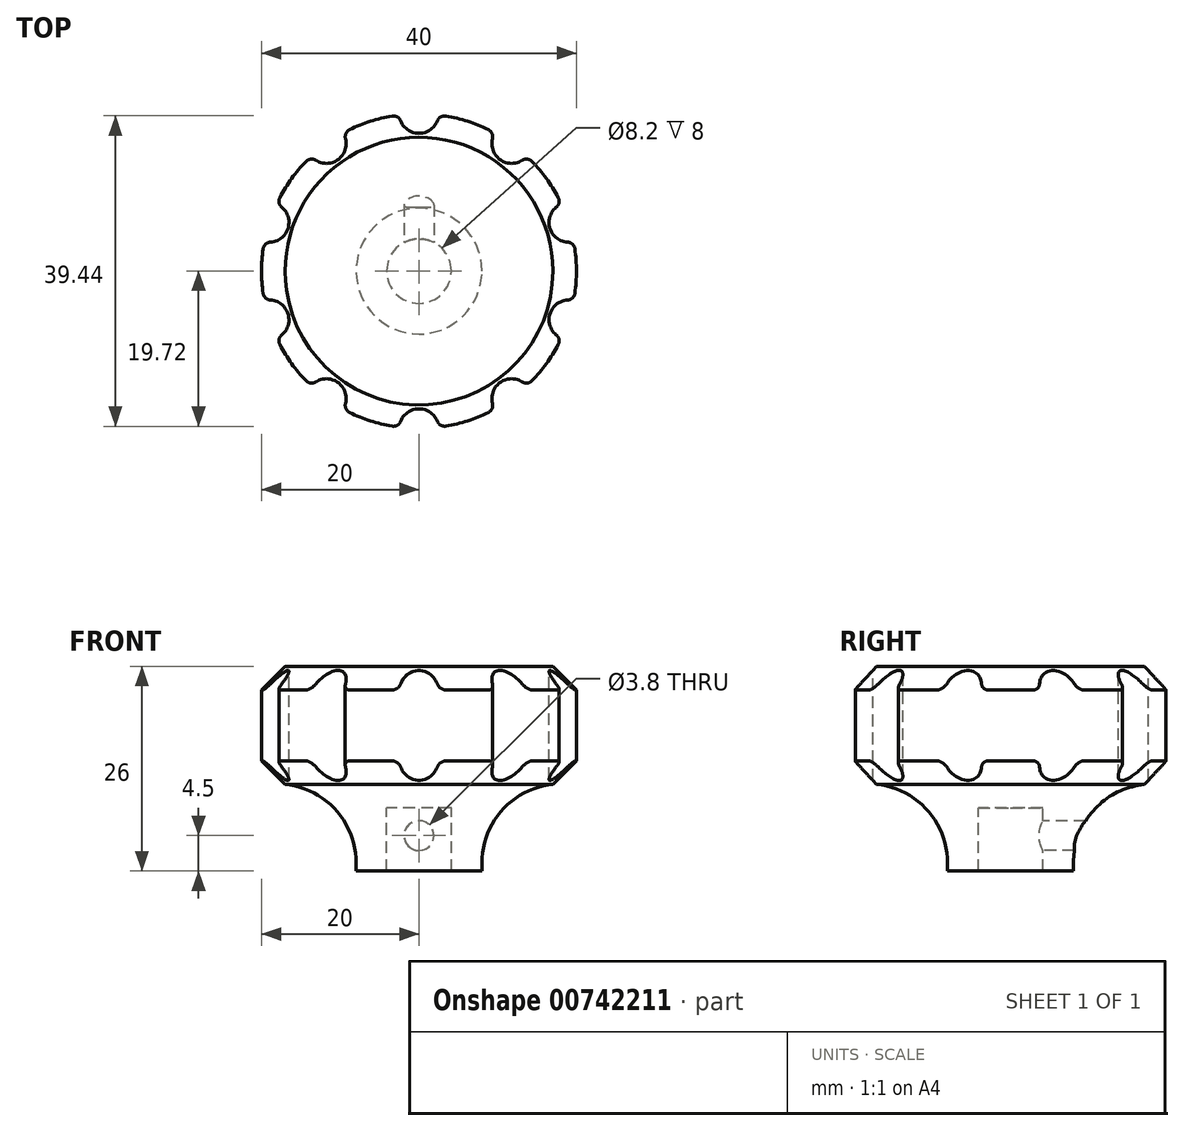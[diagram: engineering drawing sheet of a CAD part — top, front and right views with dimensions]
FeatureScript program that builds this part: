
annotation { "Feature Type Name" : "Feature", "Feature Type Description" : "" }
export const myFeature = defineFeature(function(context is Context, id is Id, definition is map)
    precondition{}
    {
        {
            var Q0;
            Q0=qCreatedBy(makeId("Front.planeOp"),FACE);
            var sketch = newSketch(context, id + "F0", { "sketchPlane" : qUnion([Q0])});
            skLineSegment(sketch, "E0", {"start": v(0, 8) * mm, "end": v(0, 26) * mm});
            skLineSegment(sketch, "E1", {"start": v(0, 26) * mm, "end": v(-20, 26) * mm});
            skLineSegment(sketch, "E2", {"start": v(-20, 26) * mm, "end": v(-20, 11) * mm});
            skLineSegment(sketch, "E3", {"start": v(-20, 11) * mm, "end": v(-8, 11) * mm});
            skLineSegment(sketch, "E4", {"start": v(-8, 11) * mm, "end": v(-8, 0) * mm});
            skLineSegment(sketch, "E5", {"start": v(-8, 0) * mm, "end": v(-4.1, 0) * mm});
            skLineSegment(sketch, "E6", {"start": v(-4.1, 0) * mm, "end": v(-4.1, 8) * mm});
            skLineSegment(sketch, "E7", {"start": v(-4.1, 8) * mm, "end": v(0, 8) * mm});
            skLineSegment(sketch, "E8", {"start": v(0, 48.85) * mm, "end": v(0, -40.92) * mm, "construction": true});
            skSolve(sketch);
        }
        {
            var Q0;
            Q0 = qSketchRegion(id + "F0", true);
            var Q1;
            Q1=sQuery(id+"F0.wireOp",EDGE,"E8");
            revolve(context, id + "F1", {"surfaceOperationType" : NewSurfaceOperationType.NEW, "entities" : qUnion([Q0]), "axis" : qUnion([Q1]), "revolveType" : RevolveType.FULL});
        }
        {
            var Q0;
            Q0=makeQuery(id+"F1.opRevolve","SWEPT_FACE",FACE,{"disambiguationData":[OSD([sQuery(id+"F0.wireOp",EDGE,"E1")])]});
            var sketch = newSketch(context, id + "F2", { "sketchPlane" : qUnion([Q0])});
            skCircle(sketch, "E9", {"center": v(0, 20) * mm, "radius": 2.5 * mm});
            skCircle(sketch, "E10.1.0", {"center": v(-11.76, 16.18) * mm, "radius": 2.5 * mm});
            skCircle(sketch, "E10.2.0", {"center": v(-19.02, 6.18) * mm, "radius": 2.5 * mm});
            skCircle(sketch, "E10.3.0", {"center": v(-19.02, -6.18) * mm, "radius": 2.5 * mm});
            skCircle(sketch, "E10.4.0", {"center": v(-11.76, -16.18) * mm, "radius": 2.5 * mm});
            skCircle(sketch, "E10.5.0", {"center": v(0, -20) * mm, "radius": 2.5 * mm});
            skCircle(sketch, "E10.6.0", {"center": v(11.76, -16.18) * mm, "radius": 2.5 * mm});
            skCircle(sketch, "E10.7.0", {"center": v(19.02, -6.18) * mm, "radius": 2.5 * mm});
            skCircle(sketch, "E10.8.0", {"center": v(19.02, 6.18) * mm, "radius": 2.5 * mm});
            skCircle(sketch, "E10.9.0", {"center": v(11.76, 16.18) * mm, "radius": 2.5 * mm});
            skPoint(sketch, "E10.center", {"position": v(0, 0) * mm});
            skSolve(sketch);
        }
        {
            var Q0;
            Q0=makeQuery(id+"F1.opRevolve","SWEPT_EDGE",EDGE,{"disambiguationData":[OSD([sQuery(id+"F0.wireOp",EDGE,"E1"),sQuery(id+"F0.wireOp",EDGE,"E2")])]});
            var Q1;
            Q1=makeQuery(id+"F1.opRevolve","SWEPT_EDGE",EDGE,{"disambiguationData":[OSD([sQuery(id+"F0.wireOp",EDGE,"E2"),sQuery(id+"F0.wireOp",EDGE,"E3")])]});
            chamfer(context, id + "F3", {"entities" : qUnion([Q0, Q1]), "width" : 3 * mm, "tangentPropagation" : true});
        }
        {
            var Q0;
            Q0 = qSketchRegion(id + "F2", true);
            extrude(context, id + "F4", {"entities" : qUnion([Q0]), "operationType" : NewBodyOperationType.REMOVE, "oppositeDirection" : true, "depth" : 25 * mm, "offsetDistance" : 25 * mm});
        }
        {
            var Q0;
            Q0=makeQuery(id+"F4.boolean.opBoolean","INTERSECT",EDGE,{"disambiguationData":[OD(0.0)],"derivedFrom":[makeQuery(id+"F1.opRevolve","SWEPT_FACE",FACE,{"disambiguationData":[OSD([sQuery(id+"F0.wireOp",EDGE,"E2")])]}),makeQuery(id+"F4.opExtrude","SWEPT_FACE",FACE,{"disambiguationData":[OSD([sQuery(id+"F2.wireOp",EDGE,"E10.4.0")])]})]});
            var Q1;
            Q1=makeQuery(id+"F4.boolean.opBoolean","INTERSECT",EDGE,{"disambiguationData":[OD(1.0)],"derivedFrom":[makeQuery(id+"F1.opRevolve","SWEPT_FACE",FACE,{"disambiguationData":[OSD([sQuery(id+"F0.wireOp",EDGE,"E2")])]}),makeQuery(id+"F4.opExtrude","SWEPT_FACE",FACE,{"disambiguationData":[OSD([sQuery(id+"F2.wireOp",EDGE,"E10.3.0")])]})]});
            var Q2;
            Q2=makeQuery(id+"F4.boolean.opBoolean","INTERSECT",EDGE,{"disambiguationData":[OD(0.0)],"derivedFrom":[makeQuery(id+"F1.opRevolve","SWEPT_FACE",FACE,{"disambiguationData":[OSD([sQuery(id+"F0.wireOp",EDGE,"E2")])]}),makeQuery(id+"F4.opExtrude","SWEPT_FACE",FACE,{"disambiguationData":[OSD([sQuery(id+"F2.wireOp",EDGE,"E10.3.0")])]})]});
            var Q3;
            Q3=makeQuery(id+"F4.boolean.opBoolean","INTERSECT",EDGE,{"disambiguationData":[OD(1.0)],"derivedFrom":[makeQuery(id+"F1.opRevolve","SWEPT_FACE",FACE,{"disambiguationData":[OSD([sQuery(id+"F0.wireOp",EDGE,"E2")])]}),makeQuery(id+"F4.opExtrude","SWEPT_FACE",FACE,{"disambiguationData":[OSD([sQuery(id+"F2.wireOp",EDGE,"E10.2.0")])]})]});
            var Q4;
            Q4=makeQuery(id+"F4.boolean.opBoolean","INTERSECT",EDGE,{"disambiguationData":[OD(0.0)],"derivedFrom":[makeQuery(id+"F1.opRevolve","SWEPT_FACE",FACE,{"disambiguationData":[OSD([sQuery(id+"F0.wireOp",EDGE,"E2")])]}),makeQuery(id+"F4.opExtrude","SWEPT_FACE",FACE,{"disambiguationData":[OSD([sQuery(id+"F2.wireOp",EDGE,"E10.2.0")])]})]});
            var Q5;
            Q5=makeQuery(id+"F4.boolean.opBoolean","INTERSECT",EDGE,{"disambiguationData":[OD(1.0)],"derivedFrom":[makeQuery(id+"F1.opRevolve","SWEPT_FACE",FACE,{"disambiguationData":[OSD([sQuery(id+"F0.wireOp",EDGE,"E2")])]}),makeQuery(id+"F4.opExtrude","SWEPT_FACE",FACE,{"disambiguationData":[OSD([sQuery(id+"F2.wireOp",EDGE,"E10.1.0")])]})]});
            var Q6;
            Q6=makeQuery(id+"F4.boolean.opBoolean","INTERSECT",EDGE,{"disambiguationData":[OD(0.0)],"derivedFrom":[makeQuery(id+"F1.opRevolve","SWEPT_FACE",FACE,{"disambiguationData":[OSD([sQuery(id+"F0.wireOp",EDGE,"E2")])]}),makeQuery(id+"F4.opExtrude","SWEPT_FACE",FACE,{"disambiguationData":[OSD([sQuery(id+"F2.wireOp",EDGE,"E10.1.0")])]})]});
            var Q7;
            Q7=makeQuery(id+"F4.boolean.opBoolean","INTERSECT",EDGE,{"disambiguationData":[OD(0.0)],"derivedFrom":[makeQuery(id+"F1.opRevolve","SWEPT_FACE",FACE,{"disambiguationData":[OSD([sQuery(id+"F0.wireOp",EDGE,"E2")])]}),makeQuery(id+"F4.opExtrude","SWEPT_FACE",FACE,{"disambiguationData":[OSD([sQuery(id+"F2.wireOp",EDGE,"E9")])]})]});
            var Q8;
            Q8=makeQuery(id+"F4.boolean.opBoolean","INTERSECT",EDGE,{"disambiguationData":[OD(1.0)],"derivedFrom":[makeQuery(id+"F1.opRevolve","SWEPT_FACE",FACE,{"disambiguationData":[OSD([sQuery(id+"F0.wireOp",EDGE,"E2")])]}),makeQuery(id+"F4.opExtrude","SWEPT_FACE",FACE,{"disambiguationData":[OSD([sQuery(id+"F2.wireOp",EDGE,"E9")])]})]});
            var Q9;
            Q9=makeQuery(id+"F4.boolean.opBoolean","INTERSECT",EDGE,{"disambiguationData":[OD(0.0)],"derivedFrom":[makeQuery(id+"F1.opRevolve","SWEPT_FACE",FACE,{"disambiguationData":[OSD([sQuery(id+"F0.wireOp",EDGE,"E2")])]}),makeQuery(id+"F4.opExtrude","SWEPT_FACE",FACE,{"disambiguationData":[OSD([sQuery(id+"F2.wireOp",EDGE,"E10.9.0")])]})]});
            var Q10;
            Q10=makeQuery(id+"F4.boolean.opBoolean","INTERSECT",EDGE,{"disambiguationData":[OD(1.0)],"derivedFrom":[makeQuery(id+"F1.opRevolve","SWEPT_FACE",FACE,{"disambiguationData":[OSD([sQuery(id+"F0.wireOp",EDGE,"E2")])]}),makeQuery(id+"F4.opExtrude","SWEPT_FACE",FACE,{"disambiguationData":[OSD([sQuery(id+"F2.wireOp",EDGE,"E10.9.0")])]})]});
            var Q11;
            Q11=makeQuery(id+"F4.boolean.opBoolean","INTERSECT",EDGE,{"disambiguationData":[OD(1.0)],"derivedFrom":[makeQuery(id+"F1.opRevolve","SWEPT_FACE",FACE,{"disambiguationData":[OSD([sQuery(id+"F0.wireOp",EDGE,"E2")])]}),makeQuery(id+"F4.opExtrude","SWEPT_FACE",FACE,{"disambiguationData":[OSD([sQuery(id+"F2.wireOp",EDGE,"E10.8.0")])]})]});
            var Q12;
            Q12=makeQuery(id+"F4.boolean.opBoolean","INTERSECT",EDGE,{"disambiguationData":[OD(0.0)],"derivedFrom":[makeQuery(id+"F1.opRevolve","SWEPT_FACE",FACE,{"disambiguationData":[OSD([sQuery(id+"F0.wireOp",EDGE,"E2")])]}),makeQuery(id+"F4.opExtrude","SWEPT_FACE",FACE,{"disambiguationData":[OSD([sQuery(id+"F2.wireOp",EDGE,"E10.8.0")])]})]});
            var Q13;
            Q13=makeQuery(id+"F4.boolean.opBoolean","INTERSECT",EDGE,{"disambiguationData":[OD(1.0)],"derivedFrom":[makeQuery(id+"F1.opRevolve","SWEPT_FACE",FACE,{"disambiguationData":[OSD([sQuery(id+"F0.wireOp",EDGE,"E2")])]}),makeQuery(id+"F4.opExtrude","SWEPT_FACE",FACE,{"disambiguationData":[OSD([sQuery(id+"F2.wireOp",EDGE,"E10.7.0")])]})]});
            var Q14;
            Q14=makeQuery(id+"F4.boolean.opBoolean","INTERSECT",EDGE,{"disambiguationData":[OD(0.0)],"derivedFrom":[makeQuery(id+"F1.opRevolve","SWEPT_FACE",FACE,{"disambiguationData":[OSD([sQuery(id+"F0.wireOp",EDGE,"E2")])]}),makeQuery(id+"F4.opExtrude","SWEPT_FACE",FACE,{"disambiguationData":[OSD([sQuery(id+"F2.wireOp",EDGE,"E10.7.0")])]})]});
            var Q15;
            Q15=makeQuery(id+"F4.boolean.opBoolean","INTERSECT",EDGE,{"disambiguationData":[OD(1.0)],"derivedFrom":[makeQuery(id+"F1.opRevolve","SWEPT_FACE",FACE,{"disambiguationData":[OSD([sQuery(id+"F0.wireOp",EDGE,"E2")])]}),makeQuery(id+"F4.opExtrude","SWEPT_FACE",FACE,{"disambiguationData":[OSD([sQuery(id+"F2.wireOp",EDGE,"E10.6.0")])]})]});
            var Q16;
            Q16=makeQuery(id+"F4.boolean.opBoolean","INTERSECT",EDGE,{"disambiguationData":[OD(0.0)],"derivedFrom":[makeQuery(id+"F1.opRevolve","SWEPT_FACE",FACE,{"disambiguationData":[OSD([sQuery(id+"F0.wireOp",EDGE,"E2")])]}),makeQuery(id+"F4.opExtrude","SWEPT_FACE",FACE,{"disambiguationData":[OSD([sQuery(id+"F2.wireOp",EDGE,"E10.6.0")])]})]});
            var Q17;
            Q17=makeQuery(id+"F4.boolean.opBoolean","INTERSECT",EDGE,{"disambiguationData":[OD(1.0)],"derivedFrom":[makeQuery(id+"F1.opRevolve","SWEPT_FACE",FACE,{"disambiguationData":[OSD([sQuery(id+"F0.wireOp",EDGE,"E2")])]}),makeQuery(id+"F4.opExtrude","SWEPT_FACE",FACE,{"disambiguationData":[OSD([sQuery(id+"F2.wireOp",EDGE,"E10.5.0")])]})]});
            var Q18;
            Q18=makeQuery(id+"F4.boolean.opBoolean","INTERSECT",EDGE,{"disambiguationData":[OD(0.0)],"derivedFrom":[makeQuery(id+"F1.opRevolve","SWEPT_FACE",FACE,{"disambiguationData":[OSD([sQuery(id+"F0.wireOp",EDGE,"E2")])]}),makeQuery(id+"F4.opExtrude","SWEPT_FACE",FACE,{"disambiguationData":[OSD([sQuery(id+"F2.wireOp",EDGE,"E10.5.0")])]})]});
            var Q19;
            Q19=makeQuery(id+"F4.boolean.opBoolean","INTERSECT",EDGE,{"disambiguationData":[OD(1.0)],"derivedFrom":[makeQuery(id+"F1.opRevolve","SWEPT_FACE",FACE,{"disambiguationData":[OSD([sQuery(id+"F0.wireOp",EDGE,"E2")])]}),makeQuery(id+"F4.opExtrude","SWEPT_FACE",FACE,{"disambiguationData":[OSD([sQuery(id+"F2.wireOp",EDGE,"E10.4.0")])]})]});
            fillet(context, id + "F5", {"entities" : qUnion([Q0, Q1, Q2, Q3, Q4, Q5, Q6, Q7, Q8, Q9, Q10, Q11, Q12, Q13, Q14, Q15, Q16, Q17, Q18, Q19]), "radius" : 1 * mm, "tangentPropagation" : true, "allowEdgeOverflow" : false});
        }
        {
            var Q0;
            Q0=makeQuery(id+"F1.opRevolve","SWEPT_EDGE",EDGE,{"disambiguationData":[OSD([sQuery(id+"F0.wireOp",EDGE,"E3"),sQuery(id+"F0.wireOp",EDGE,"E4")])]});
            fillet(context, id + "F6", {"entities" : qUnion([Q0]), "radius" : 10 * mm, "tangentPropagation" : true, "allowEdgeOverflow" : false});
        }
        {
            var Q0;
            Q0=qCreatedBy(makeId("Front.planeOp"),FACE);
            var sketch = newSketch(context, id + "F7", { "sketchPlane" : qUnion([Q0])});
            skCircle(sketch, "E11", {"center": v(0, 4.5) * mm, "radius": 1.9 * mm});
            skSolve(sketch);
        }
        {
            var Q0;
            Q0 = qSketchRegion(id + "F7", true);
            extrude(context, id + "F8", {"entities" : qUnion([Q0]), "operationType" : NewBodyOperationType.REMOVE, "oppositeDirection" : true, "depth" : 25 * mm, "offsetDistance" : 25 * mm});
        }
    });
